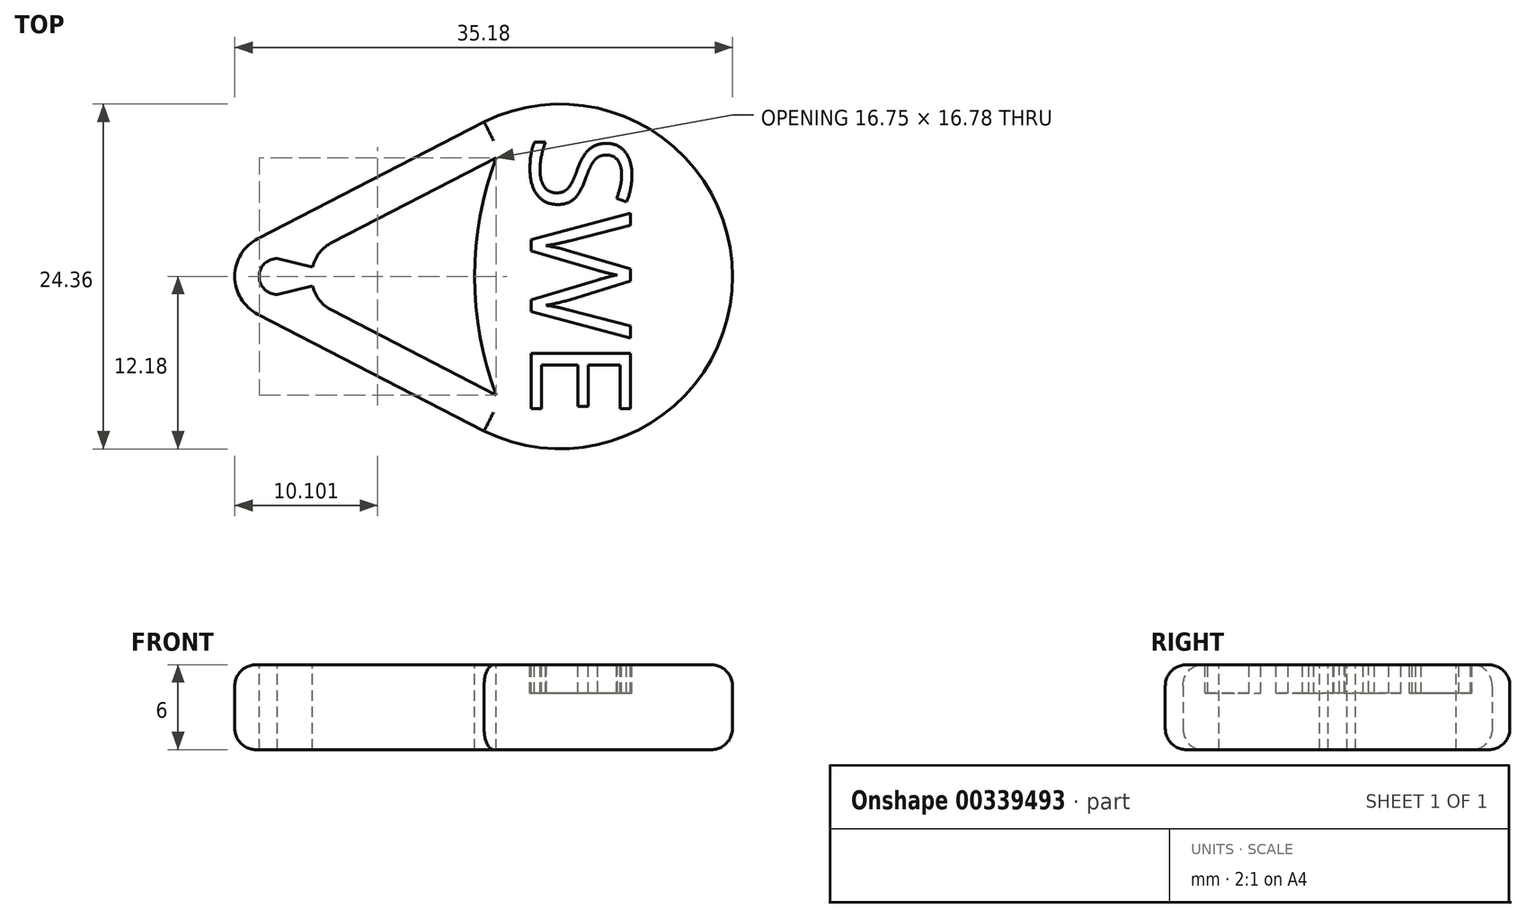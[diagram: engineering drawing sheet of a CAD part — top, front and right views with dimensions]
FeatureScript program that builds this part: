
annotation { "Feature Type Name" : "Feature", "Feature Type Description" : "" }
export const myFeature = defineFeature(function(context is Context, id is Id, definition is map)
    precondition{}
    {
        {
            var Q0;
            Q0=qCreatedBy(makeId("Top.planeOp"),FACE);
            var sketch = newSketch(context, id + "F0", { "sketchPlane" : qUnion([Q0])});
            skCircle(sketch, "E0", {"center": v(0, 0) * mm, "radius": 3 * mm});
            skLineSegment(sketch, "E1", {"start": v(-1.38, 2.67) * mm, "end": v(14.62, 10.92) * mm});
            skLineSegment(sketch, "E2", {"start": v(-1.38, -2.67) * mm, "end": v(14.62, -10.92) * mm});
            skPoint(sketch, "E3.orphan", {"position": v(20, 13.7) * mm});
            skArc(sketch, "E4.trimOffspring", {"start": v(14.62, -10.92) * mm, "mid": v(32.18, 0) * mm, "end": v(14.62, 10.92) * mm});
            skPoint(sketch, "E5.end.orphan", {"position": v(20, -13.7) * mm});
            skLineSegment(sketch, "E6", {"start": v(20, 28.47) * mm, "end": v(20, -22.67) * mm, "construction": true});
            skSolve(sketch);
        }
        {
            var Q0;
            Q0=qSketchRegion(id+"F0",true);
            extrude(context, id + "F1", {"entities" : qUnion([Q0]), "depth" : 3 * mm, "hasSecondDirection" : true, "secondDirectionOppositeDirection" : true, "secondDirectionDepth" : 3 * mm});
        }
        {
            var Q0;
            Q0=qCreatedBy(makeId("Top.planeOp"),FACE);
            var sketch = newSketch(context, id + "F2", { "sketchPlane" : qUnion([Q0])});
            skLineSegment(sketch, "E7", {"start": v(3.88, 2.4) * mm, "end": v(15.48, 8.4) * mm});
            skLineSegment(sketch, "E8", {"start": v(3.88, -2.4) * mm, "end": v(15.48, -8.4) * mm});
            skArc(sketch, "E9", {"start": v(3.88, 2.4) * mm, "mid": v(2.41, 0) * mm, "end": v(3.88, -2.4) * mm});
            skArc(sketch, "E10", {"start": v(15.48, 8.4) * mm, "mid": v(13.96, 0) * mm, "end": v(15.48, -8.4) * mm});
            skSolve(sketch);
        }
        {
            var Q0;
            Q0=qSketchRegion(id+"F2",true);
            var Q1;
            Q1=makeQuery(id+"F1.opExtrude","CAP_FACE",FACE,{"disambiguationData":[OSD([sQuery(id+"F0.wireOp",EDGE,"E0"),sQuery(id+"F0.wireOp",EDGE,"E5"),sQuery(id+"F0.wireOp",EDGE,"E1"),sQuery(id+"F0.wireOp",EDGE,"E2")])],"isStart":true});
            var Q2;
            Q2=makeQuery(id+"F1.opExtrude","CAP_FACE",FACE,{"disambiguationData":[OSD([sQuery(id+"F0.wireOp",EDGE,"E0"),sQuery(id+"F0.wireOp",EDGE,"E5"),sQuery(id+"F0.wireOp",EDGE,"E1"),sQuery(id+"F0.wireOp",EDGE,"E2")])],"isStart":false});
            extrude(context, id + "F3", {"entities" : qUnion([Q0]), "operationType" : NewBodyOperationType.REMOVE, "endBound" : BoundingType.UP_TO_SURFACE, "oppositeDirection" : true, "endBoundEntityFace" : qUnion([Q1]), "depth" : 25 * mm, "hasSecondDirection" : true, "secondDirectionBound" : SecondDirectionBoundingType.UP_TO_SURFACE, "secondDirectionOppositeDirection" : false, "secondDirectionBoundEntityFace" : qUnion([Q2]), "secondDirectionDepth" : 25 * mm});
        }
        {
            var Q0;
            Q0=makeQuery(id+"F1.opExtrude","CAP_FACE",FACE,{"disambiguationData":[OSD([sQuery(id+"F0.wireOp",EDGE,"E0"),sQuery(id+"F0.wireOp",EDGE,"E5"),sQuery(id+"F0.wireOp",EDGE,"E1"),sQuery(id+"F0.wireOp",EDGE,"E2")])],"isStart":false});
            var sketch = newSketch(context, id + "F4", { "sketchPlane" : qUnion([Q0])});
            skArc(sketch, "E11", {"start": v(0, 1.27) * mm, "mid": v(-1.27, 0) * mm, "end": v(0, -1.27) * mm});
            skLineSegment(sketch, "E12", {"start": v(0, -1.28) * mm, "end": v(5.24, 0) * mm});
            skLineSegment(sketch, "E13", {"start": v(5.24, 0) * mm, "end": v(0, 1.27) * mm});
            skSolve(sketch);
        }
        {
            var Q0;
            Q0=qSketchRegion(id+"F4",true);
            var Q1;
            Q1=makeQuery(id+"F1.opExtrude","CAP_FACE",FACE,{"disambiguationData":[OSD([sQuery(id+"F0.wireOp",EDGE,"E0"),sQuery(id+"F0.wireOp",EDGE,"E5"),sQuery(id+"F0.wireOp",EDGE,"E1"),sQuery(id+"F0.wireOp",EDGE,"E2")])],"isStart":true});
            extrude(context, id + "F5", {"entities" : qUnion([Q0]), "operationType" : NewBodyOperationType.REMOVE, "endBound" : BoundingType.UP_TO_SURFACE, "oppositeDirection" : true, "endBoundEntityFace" : qUnion([Q1]), "depth" : 25 * mm});
        }
        {
            var Q0;
            Q0=makeQuery(id+"F1.opExtrude","CAP_FACE",FACE,{"disambiguationData":[OSD([sQuery(id+"F0.wireOp",EDGE,"E0"),sQuery(id+"F0.wireOp",EDGE,"E5"),sQuery(id+"F0.wireOp",EDGE,"E1"),sQuery(id+"F0.wireOp",EDGE,"E2")])],"isStart":false});
            var sketch = newSketch(context, id + "F6", { "sketchPlane" : qUnion([Q0])});
            skText(sketch, "E14", { "text": "SWE", "fontName": "OpenSans-Regular.ttf"});
            const initialGuessF6  = {"E14": [0.01796, 0.01, 0, -1, 0.00707]};
            skSetInitialGuess(sketch, initialGuessF6);
            skSolve(sketch);
        }
        {
            var Q0;
            Q0=qSketchRegion(id+"F6",true);
            extrude(context, id + "F7", {"entities" : qUnion([Q0]), "operationType" : NewBodyOperationType.REMOVE, "oppositeDirection" : true, "depth" : 2 * mm});
        }
        {
            var Q0;
            Q0=makeQuery(id+"F1.opExtrude","CAP_EDGE",EDGE,{"disambiguationData":[OSD([sQuery(id+"F0.wireOp",EDGE,"E1")])],"isStart":false});
            var Q1;
            Q1=makeQuery(id+"F1.opExtrude","CAP_EDGE",EDGE,{"disambiguationData":[OSD([sQuery(id+"F0.wireOp",EDGE,"E4.trimOffspring")])],"isStart":false});
            var Q2;
            Q2=makeQuery(id+"F1.opExtrude","CAP_EDGE",EDGE,{"disambiguationData":[OSD([sQuery(id+"F0.wireOp",EDGE,"E2")])],"isStart":true});
            var Q3;
            Q3=makeQuery(id+"F1.opExtrude","CAP_EDGE",EDGE,{"disambiguationData":[OSD([sQuery(id+"F0.wireOp",EDGE,"E4.trimOffspring")])],"isStart":true});
            fillet(context, id + "F8", {"entities" : qUnion([Q0, Q1, Q2, Q3]), "radius" : 1.5 * mm, "tangentPropagation" : true, "allowEdgeOverflow" : false});
        }
    });
